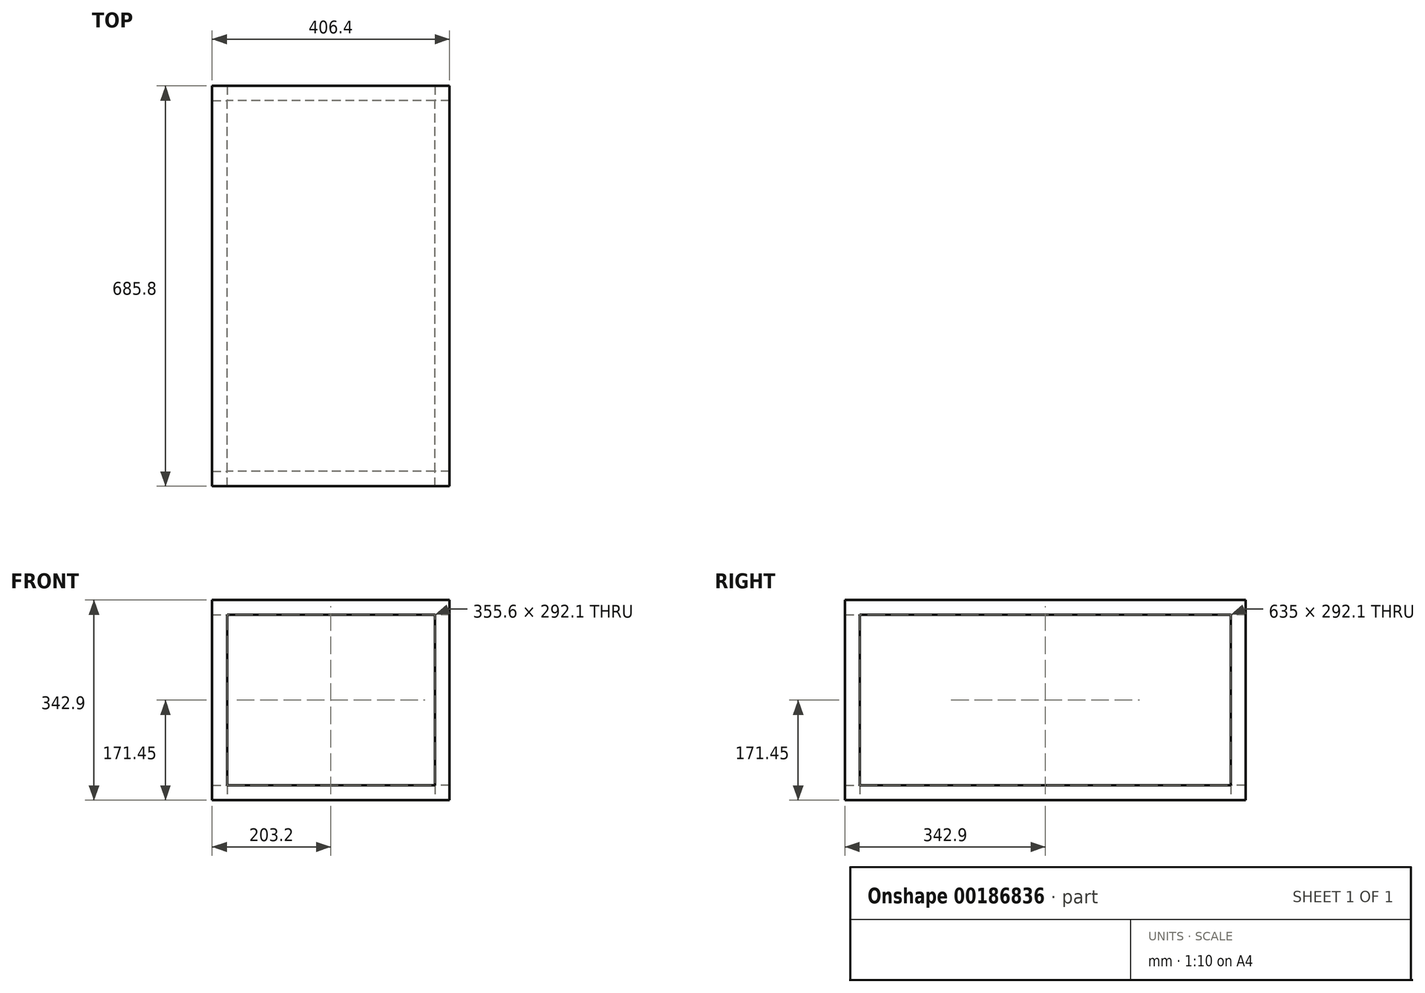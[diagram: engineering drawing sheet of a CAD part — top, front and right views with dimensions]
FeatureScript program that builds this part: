
annotation { "Feature Type Name" : "Feature", "Feature Type Description" : "" }
export const myFeature = defineFeature(function(context is Context, id is Id, definition is map)
    precondition{}
    {
        {
            var Q0;
            Q0=qCreatedBy(makeId("Top.planeOp"),FACE);
            var sketch = newSketch(context, id + "F0", { "sketchPlane" : qUnion([Q0])});
            skLineSegment(sketch, "E0.bottom", {"start": v(203.2, 342.9) * mm, "end": v(-203.2, 342.9) * mm});
            skLineSegment(sketch, "E0.top", {"start": v(203.2, -342.9) * mm, "end": v(-203.2, -342.9) * mm});
            skLineSegment(sketch, "E0.left", {"start": v(203.2, 342.9) * mm, "end": v(203.2, -342.9) * mm});
            skLineSegment(sketch, "E0.right", {"start": v(-203.2, 342.9) * mm, "end": v(-203.2, -342.9) * mm});
            skPoint(sketch, "E0.middle", {"position": v(0, 0) * mm});
            skSolve(sketch);
        }
        {
            var Q0;
            Q0 = qSketchRegion(id + "F0", true);
            extrude(context, id + "F1", {"entities" : qUnion([Q0]), "depth" : 25.4 * mm});
        }
        {
            var Q0;
            Q0=makeQuery(id+"F1.opExtrude","CAP_FACE",FACE,{"disambiguationData":[OSD([sQuery(id+"F0.wireOp",EDGE,"E0.bottom"),sQuery(id+"F0.wireOp",EDGE,"E0.top"),sQuery(id+"F0.wireOp",EDGE,"E0.left"),sQuery(id+"F0.wireOp",EDGE,"E0.right")])],"isStart":true});
            var sketch = newSketch(context, id + "F2", { "sketchPlane" : qUnion([Q0])});
            skLineSegment(sketch, "E1.bottom", {"start": v(203.2, 342.9) * mm, "end": v(177.8, 342.9) * mm});
            skLineSegment(sketch, "E1.top", {"start": v(203.2, 317.5) * mm, "end": v(177.8, 317.5) * mm});
            skLineSegment(sketch, "E1.left", {"start": v(203.2, 342.9) * mm, "end": v(203.2, 317.5) * mm});
            skLineSegment(sketch, "E1.right", {"start": v(177.8, 342.9) * mm, "end": v(177.8, 317.5) * mm});
            skLineSegment(sketch, "E2.bottom", {"start": v(-203.2, -342.9) * mm, "end": v(-177.8, -342.9) * mm});
            skLineSegment(sketch, "E2.top", {"start": v(-203.2, -317.5) * mm, "end": v(-177.8, -317.5) * mm});
            skLineSegment(sketch, "E2.left", {"start": v(-203.2, -342.9) * mm, "end": v(-203.2, -317.5) * mm});
            skLineSegment(sketch, "E2.right", {"start": v(-177.8, -342.9) * mm, "end": v(-177.8, -317.5) * mm});
            skLineSegment(sketch, "E3.bottom", {"start": v(203.2, -342.9) * mm, "end": v(177.8, -342.9) * mm});
            skLineSegment(sketch, "E3.top", {"start": v(203.2, -317.5) * mm, "end": v(177.8, -317.5) * mm});
            skLineSegment(sketch, "E3.left", {"start": v(203.2, -342.9) * mm, "end": v(203.2, -317.5) * mm});
            skLineSegment(sketch, "E3.right", {"start": v(177.8, -342.9) * mm, "end": v(177.8, -317.5) * mm});
            skLineSegment(sketch, "E4.bottom", {"start": v(-203.2, 342.9) * mm, "end": v(-177.8, 342.9) * mm});
            skLineSegment(sketch, "E4.top", {"start": v(-203.2, 317.5) * mm, "end": v(-177.8, 317.5) * mm});
            skLineSegment(sketch, "E4.left", {"start": v(-203.2, 342.9) * mm, "end": v(-203.2, 317.5) * mm});
            skLineSegment(sketch, "E4.right", {"start": v(-177.8, 342.9) * mm, "end": v(-177.8, 317.5) * mm});
            skSolve(sketch);
        }
        {
            var Q0;
            Q0 = qSketchRegion(id + "F2", true);
            extrude(context, id + "F3", {"entities" : qUnion([Q0]), "operationType" : NewBodyOperationType.ADD, "depth" : 317.5 * mm});
        }
        {
            var Q0;
            Q0=makeQuery(id+"F3.opExtrude","CAP_FACE",FACE,{"disambiguationData":[OSD([sQuery(id+"F2.wireOp",EDGE,"E4.bottom"),sQuery(id+"F2.wireOp",EDGE,"E4.top"),sQuery(id+"F2.wireOp",EDGE,"E4.left"),sQuery(id+"F2.wireOp",EDGE,"E4.right")])],"isStart":false});
            var sketch = newSketch(context, id + "F4", { "sketchPlane" : qUnion([Q0])});
            skLineSegment(sketch, "E5.bottom", {"start": v(-203.2, 342.9) * mm, "end": v(203.2, 342.9) * mm});
            skLineSegment(sketch, "E5.top", {"start": v(-203.2, -342.9) * mm, "end": v(203.2, -342.9) * mm});
            skLineSegment(sketch, "E5.left", {"start": v(-203.2, 342.9) * mm, "end": v(-203.2, -342.9) * mm});
            skLineSegment(sketch, "E5.right", {"start": v(203.2, 342.9) * mm, "end": v(203.2, -342.9) * mm});
            skSolve(sketch);
        }
        {
            var Q0;
            Q0 = qSketchRegion(id + "F4", true);
            extrude(context, id + "F5", {"entities" : qUnion([Q0]), "operationType" : NewBodyOperationType.ADD, "oppositeDirection" : true, "depth" : 25.4 * mm});
        }
        {
            var Q0;
            Q0=makeQuery(id+"F5.boolean.opBoolean","MERGE",FACE,{"derivedFrom":[makeQuery(id+"F3.opExtrude","CAP_FACE",FACE,{"disambiguationData":[OSD([sQuery(id+"F2.wireOp",EDGE,"E1.bottom"),sQuery(id+"F2.wireOp",EDGE,"E1.top"),sQuery(id+"F2.wireOp",EDGE,"E1.left"),sQuery(id+"F2.wireOp",EDGE,"E1.right")])],"isStart":false}),makeQuery(id+"F3.opExtrude","CAP_FACE",FACE,{"disambiguationData":[OSD([sQuery(id+"F2.wireOp",EDGE,"E2.bottom"),sQuery(id+"F2.wireOp",EDGE,"E2.top"),sQuery(id+"F2.wireOp",EDGE,"E2.left"),sQuery(id+"F2.wireOp",EDGE,"E2.right")])],"isStart":false}),makeQuery(id+"F3.opExtrude","CAP_FACE",FACE,{"disambiguationData":[OSD([sQuery(id+"F2.wireOp",EDGE,"E3.bottom"),sQuery(id+"F2.wireOp",EDGE,"E3.top"),sQuery(id+"F2.wireOp",EDGE,"E3.left"),sQuery(id+"F2.wireOp",EDGE,"E3.right")])],"isStart":false}),makeQuery(id+"F3.opExtrude","CAP_FACE",FACE,{"disambiguationData":[OSD([sQuery(id+"F2.wireOp",EDGE,"E4.bottom"),sQuery(id+"F2.wireOp",EDGE,"E4.top"),sQuery(id+"F2.wireOp",EDGE,"E4.left"),sQuery(id+"F2.wireOp",EDGE,"E4.right")])],"isStart":false}),makeQuery(id+"F5.opExtrude","CAP_FACE",FACE,{"disambiguationData":[OSD([sQuery(id+"F4.wireOp",EDGE,"E5.bottom"),sQuery(id+"F4.wireOp",EDGE,"E5.top"),sQuery(id+"F4.wireOp",EDGE,"E5.left"),sQuery(id+"F4.wireOp",EDGE,"E5.right")])],"isStart":true})]});
            var sketch = newSketch(context, id + "F6", { "sketchPlane" : qUnion([Q0])});
            skLineSegment(sketch, "E6.bottom", {"start": v(177.8, 317.5) * mm, "end": v(-177.8, 317.5) * mm});
            skLineSegment(sketch, "E6.top", {"start": v(177.8, -317.5) * mm, "end": v(-177.8, -317.5) * mm});
            skLineSegment(sketch, "E6.left", {"start": v(177.8, 317.5) * mm, "end": v(177.8, -317.5) * mm});
            skLineSegment(sketch, "E6.right", {"start": v(-177.8, 317.5) * mm, "end": v(-177.8, -317.5) * mm});
            skPoint(sketch, "E6.middle", {"position": v(0, 0) * mm});
            skSolve(sketch);
        }
        {
            var Q0;
            Q0 = qSketchRegion(id + "F6", true);
            extrude(context, id + "F7", {"entities" : qUnion([Q0]), "operationType" : NewBodyOperationType.REMOVE, "oppositeDirection" : true, "depth" : 25.4 * mm});
        }
    });
